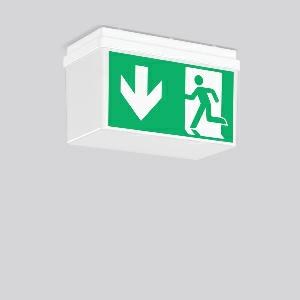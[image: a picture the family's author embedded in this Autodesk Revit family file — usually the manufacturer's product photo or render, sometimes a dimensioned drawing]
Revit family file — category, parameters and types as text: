
# Revit family: gsun_3_672521_002_07_a22e
name_source: partatom
category: Lighting Fixtures
units: mm (PartAtom-declared; Revit-internal decimal feet)

## family parameters
Cut with Voids When Loaded = No
Host = Face
Light Source = No
Part Type = Normal
Room Calculation Point = No
Round Connector Dimension = Use Diameter
Shared = No

## types (1)
- GSUN 3 (1 x LED Modul 840, 200 lm, 4000)
    Apparent Load = 4 VA
    Approval mark = CE
    CIE Flux Codes = 31 59 82 69 100
    Color Rendering = 80
    Color Temperature = 4000
    Default Elevation = 1800 mm
    Description = Series: GSUN 3
Luminaire for escape route identification. Base: plastic Diffuser: plastic, opal 4 plastic foils with escape route motifs included (ISO 7010). Suitable for Ceiling mounting, Wall (surface). Pendant luminaire also possible with accessories. Electronic ballast included. Self-contained system with automatic self-test and feedback via DALI bus, only to RZB DALI monitoring system. 
Colour: white
Length: 241 mm
Width: 126 mm
Height: 147 mm
Weight: 440 g
Operating mode: maintained power mode
Viewing Distance: 21 m
Duration time: 8 h
Lamp: LED
Socket: without socket
Colour temperature: 4000K
Colour rendering index (CRI): 80
System power: 4 W
Control gear: EB
Protection class: II
Type of protection: IP 54
    Height = 147 mm
    Lamp = 1 x LED Modul 840
    Lamp Light Flux = 200 lm
    Lamp count = 1
    Length = 241 mm
    Lifetime = 50000 h
    Luminous efficacy = 51 lm/W
    Manufacturer = RZB
    ModVariant = No
    Model = 672521.002.07
    Mounting Place = Ceiling, Wall
    Mounting Type = Surface mounted
    Number of Poles = 1
    OnlyDefault = Yes
    Power Factor = 1
    Product Name = GSUN 3
    Product group = Surface mounted ceiling and wall luminaires
    ProductGroupID = 305
    Protection Class = Protection class II
    Protection Degree = IP 54
    RLX_Detail_Level = 1
    RLX_Emergency_Light_Flux = 40 lm
    RLX_Emergency_Type = 3
    RLX_Emergency_Type_DB = Yes
    RlxData = <blob elided: 40589 chars, md5=9b36066b>
    Socket = socket
    Standby Power = 0 W
    System Light Flux = 200 lm
    System Power = 4 W
    Type Comments = Product without accessories
    Type Image = 672520.002.jpg
    URL = http://relux.com
    VarID = ---
    Voltage = 230 V
    Voltage Range = 220-240 V
    Weight = 0.00 kg
    Width = 126 mm

## geometry (parser evidence)
native form markers: Blend x4, Sweep x14
no freeform markers — native parametric forms only
